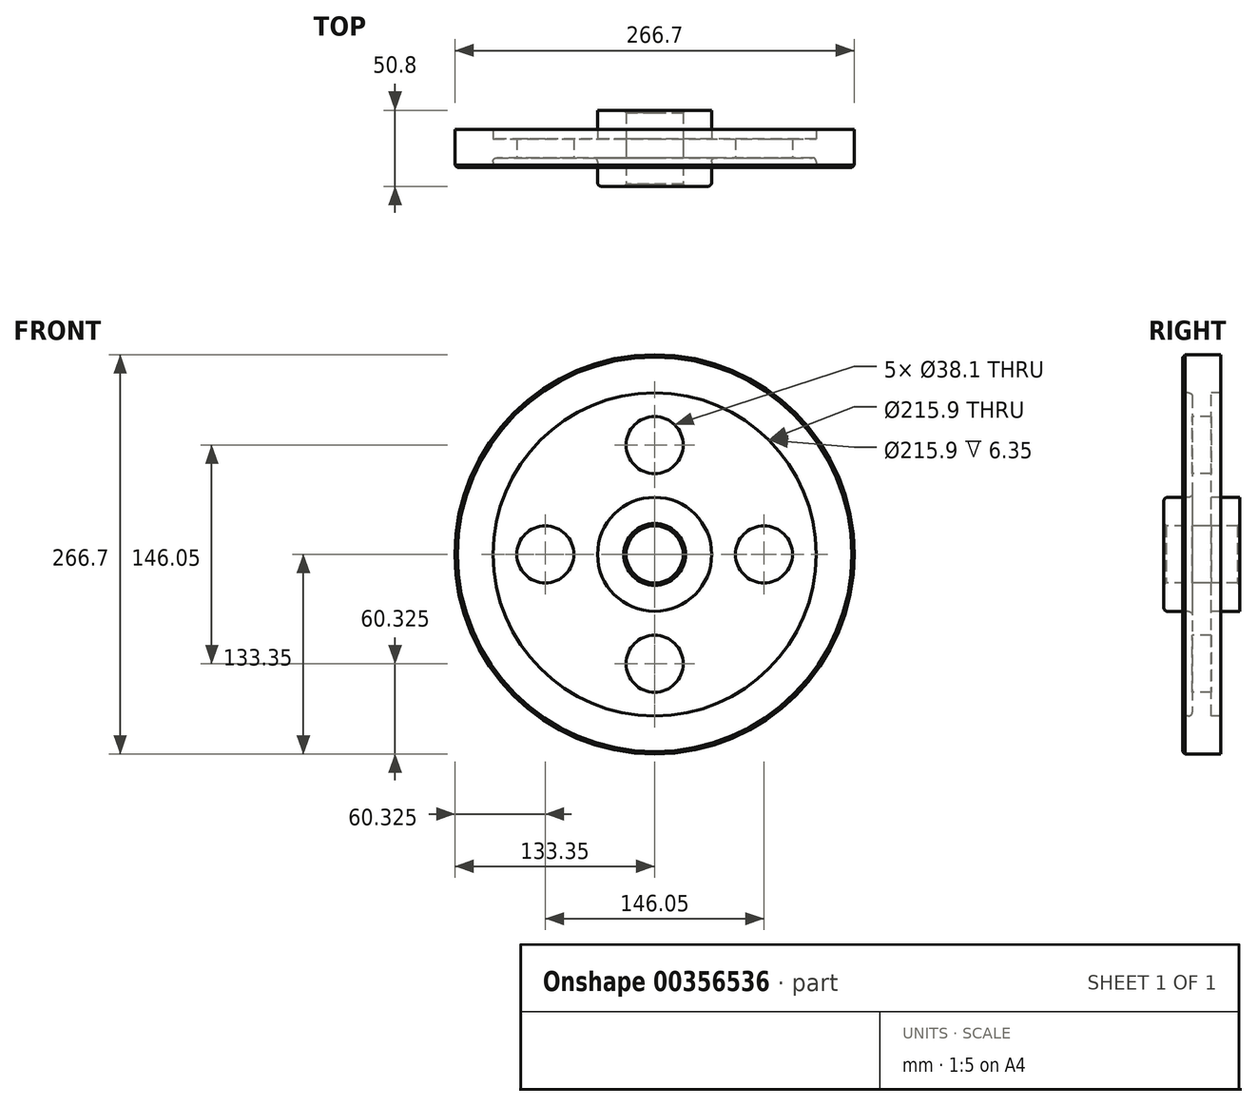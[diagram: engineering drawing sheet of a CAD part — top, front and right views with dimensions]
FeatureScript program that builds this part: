
annotation { "Feature Type Name" : "Feature", "Feature Type Description" : "" }
export const myFeature = defineFeature(function(context is Context, id is Id, definition is map)
    precondition{}
    {
        {
            var Q0;
            Q0=qCreatedBy(makeId("Right.planeOp"),FACE);
            var sketch = newSketch(context, id + "F0", { "sketchPlane" : qUnion([Q0])});
            skLineSegment(sketch, "E0", {"start": v(0, 0) * mm, "end": v(25.4, 0) * mm});
            skLineSegment(sketch, "E1.0", {"start": v(12.7, 19.05) * mm, "end": v(25.4, 19.05) * mm});
            skLineSegment(sketch, "E2.0", {"start": v(6.35, 107.95) * mm, "end": v(12.7, 107.95) * mm});
            skLineSegment(sketch, "E3.0", {"start": v(0, 133.35) * mm, "end": v(12.7, 133.35) * mm});
            skLineSegment(sketch, "E4.0", {"start": v(6.35, 38.1) * mm, "end": v(25.4, 38.1) * mm});
            skLineSegment(sketch, "E5.0", {"start": v(12.7, 133.35) * mm, "end": v(12.7, 107.95) * mm});
            skLineSegment(sketch, "E6", {"start": v(0, 0) * mm, "end": v(0, 8.2) * mm});
            skLineSegment(sketch, "E7", {"start": v(0, 133.35) * mm, "end": v(0, 19.05) * mm});
            skLineSegment(sketch, "E8.0", {"start": v(6.35, 107.95) * mm, "end": v(6.35, 38.1) * mm});
            skLineSegment(sketch, "E9.trimOffspring", {"start": v(25.4, 38.1) * mm, "end": v(25.4, 19.05) * mm});
            skLineSegment(sketch, "E10", {"start": v(12.7, 19.05) * mm, "end": v(0, 19.05) * mm});
            skLineSegment(sketch, "E11.trimOffspring", {"start": v(0, 8.2) * mm, "end": v(0, 0) * mm});
            skLineSegment(sketch, "E12.MirrorCS", {"start": v(-12.7, 133.35) * mm, "end": v(-12.7, 107.95) * mm});
            skLineSegment(sketch, "E13.MirrorCS", {"start": v(0, 133.35) * mm, "end": v(-12.7, 133.35) * mm});
            skLineSegment(sketch, "E14.MirrorCS", {"start": v(-6.35, 107.95) * mm, "end": v(-12.7, 107.95) * mm});
            skLineSegment(sketch, "E15.MirrorCS", {"start": v(-6.35, 107.95) * mm, "end": v(-6.35, 38.1) * mm});
            skLineSegment(sketch, "E16.MirrorCS", {"start": v(-6.35, 38.1) * mm, "end": v(-25.4, 38.1) * mm});
            skLineSegment(sketch, "E17.MirrorCS", {"start": v(-25.4, 38.1) * mm, "end": v(-25.4, 19.05) * mm});
            skLineSegment(sketch, "E18.MirrorCS", {"start": v(-12.7, 19.05) * mm, "end": v(-25.4, 19.05) * mm});
            skLineSegment(sketch, "E19.MirrorCS", {"start": v(-12.7, 19.05) * mm, "end": v(0, 19.05) * mm});
            skSolve(sketch);
        }
        {
            var Q0;
            Q0 = qSketchRegion(id + "F0", true);
            var Q1;
            Q1=sQuery(id+"F0.wireOp",EDGE,"E0");
            revolve(context, id + "F1", {"entities" : qUnion([Q0]), "axis" : qUnion([Q1]), "revolveType" : RevolveType.FULL});
        }
        {
            var Q0;
            Q0=makeQuery(id+"F1.opRevolve","SWEPT_FACE",FACE,{"disambiguationData":[OSD([sQuery(id+"F0.wireOp",EDGE,"E15.MirrorCS")])]});
            var sketch = newSketch(context, id + "F2", { "sketchPlane" : qUnion([Q0])});
            skCircle(sketch, "E20", {"center": v(0, 73.03) * mm, "radius": 19.05 * mm});
            skCircle(sketch, "E21.1.0", {"center": v(-73.03, 0) * mm, "radius": 19.05 * mm});
            skCircle(sketch, "E21.2.0", {"center": v(0, -73.03) * mm, "radius": 19.05 * mm});
            skPoint(sketch, "E21.center", {"position": v(0, 0) * mm});
            skCircle(sketch, "E22.1.3.0", {"center": v(73.03, 0) * mm, "radius": 19.05 * mm});
            skSolve(sketch);
        }
        {
            var Q0;
            Q0=makeQuery(id+"F2.imprint","IMPRINT",FACE,{"disambiguationData":[TD([[makeQuery(id+"F2.imprint","IMPRINT",EDGE,{"derivedFrom":sQuery(id+"F2.wireOp",EDGE,"E21.1.0")}),1.0]])]});
            var Q1;
            Q1=makeQuery(id+"F2.imprint","IMPRINT",FACE,{"disambiguationData":[TD([[makeQuery(id+"F2.imprint","IMPRINT",EDGE,{"derivedFrom":sQuery(id+"F2.wireOp",EDGE,"E20")}),1.0]])]});
            var Q2;
            Q2=makeQuery(id+"F2.imprint","IMPRINT",FACE,{"disambiguationData":[TD([[makeQuery(id+"F2.imprint","IMPRINT",EDGE,{"derivedFrom":sQuery(id+"F2.wireOp",EDGE,"E22.1.3.0")}),1.0]])]});
            var Q3;
            Q3=makeQuery(id+"F2.imprint","IMPRINT",FACE,{"disambiguationData":[TD([[makeQuery(id+"F2.imprint","IMPRINT",EDGE,{"derivedFrom":sQuery(id+"F2.wireOp",EDGE,"E21.2.0")}),1.0]])]});
            extrude(context, id + "F3", {"entities" : qUnion([Q0, Q1, Q2, Q3]), "operationType" : NewBodyOperationType.REMOVE, "oppositeDirection" : true, "depth" : 25.4 * mm});
        }
        {
            var Q0;
            Q0=makeQuery(id+"F1.opRevolve","SWEPT_EDGE",EDGE,{"disambiguationData":[OSD([sQuery(id+"F0.wireOp",EDGE,"E14.MirrorCS"),sQuery(id+"F0.wireOp",EDGE,"E15.MirrorCS")])]});
            var Q1;
            Q1=makeQuery(id+"F1.opRevolve","SWEPT_EDGE",EDGE,{"disambiguationData":[OSD([sQuery(id+"F0.wireOp",EDGE,"E12.MirrorCS"),sQuery(id+"F0.wireOp",EDGE,"E14.MirrorCS")])]});
            var Q2;
            Q2=makeQuery(id+"F1.opRevolve","SWEPT_EDGE",EDGE,{"disambiguationData":[OSD([sQuery(id+"F0.wireOp",EDGE,"E15.MirrorCS"),sQuery(id+"F0.wireOp",EDGE,"E16.MirrorCS")])]});
            var Q3;
            Q3=makeQuery(id+"F1.opRevolve","SWEPT_EDGE",EDGE,{"disambiguationData":[OSD([sQuery(id+"F0.wireOp",EDGE,"E16.MirrorCS"),sQuery(id+"F0.wireOp",EDGE,"E17.MirrorCS")])]});
            fillet(context, id + "F4", {"entities" : qUnion([Q0, Q1, Q2, Q3]), "radius" : 2.54 * mm, "tangentPropagation" : true, "allowEdgeOverflow" : false});
        }
        {
            var Q0;
            Q0=makeQuery(id+"F1.opRevolve","SWEPT_EDGE",EDGE,{"disambiguationData":[OSD([sQuery(id+"F0.wireOp",EDGE,"E17.MirrorCS"),sQuery(id+"F0.wireOp",EDGE,"E18.MirrorCS")])]});
            var Q1;
            Q1=makeQuery(id+"F1.opRevolve","SWEPT_EDGE",EDGE,{"disambiguationData":[OSD([sQuery(id+"F0.wireOp",EDGE,"E13.MirrorCS"),sQuery(id+"F0.wireOp",EDGE,"E12.MirrorCS")])]});
            var Q2;
            Q2=makeQuery(id+"F1.opRevolve","SWEPT_EDGE",EDGE,{"disambiguationData":[OSD([sQuery(id+"F0.wireOp",EDGE,"E1.0"),sQuery(id+"F0.wireOp",EDGE,"E9.trimOffspring")])]});
            chamfer(context, id + "F5", {"entities" : qUnion([Q0, Q1, Q2]), "width" : 1.59 * mm, "tangentPropagation" : true});
        }
    });
